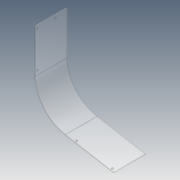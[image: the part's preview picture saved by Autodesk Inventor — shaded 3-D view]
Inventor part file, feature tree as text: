
AUTODESK INVENTOR PART (.ipt)
format: ipt  version: 2012 (Build 160160000, 160)  size: 96,256 bytes
history: native  units: in
note: dims shown in document units (in); Inventor stores cm internally (conversion verified against a paired STEP export)
features: pattern_linear x3, hole x2, extrude x1, sketch x1, reference x1
ambient origin geometry x8: Origin, YZ Plane, XZ Plane, XY Plane, X Axis, Y Axis, Z Axis, Center Point
bodies: Solid1 (feature_tree)
feature tree (8):
  extrude  "Extrusion1"  Depth=0.5in
  hole  "Hole1"  [1 undecoded]
  pattern_linear  "Rectangular Pattern1"  Count1=2 Spacing1=2.6875in
  pattern_linear  "Rectangular Pattern2"  Spacing1=0.5in  [1 undecoded]
  hole  "Hole2"  [1 undecoded]
  pattern_linear  "Rectangular Pattern4"  [2 undecoded]
  sketch  "Sketch1"  dims[d0=4.625in d1=0.0in d2=0.5in d3=0.3125in d4=0.265in d5=0.75in d6=0.375in d7=0.25in d8=0.5635in d9=1.0in d10=0.8108in d11=0.7874in d13=5.25in d14=0.7874in d16=2.6875in d17=0.5in d18=0.3125in d19=0.265in d20=0.75in d21=0.375in d22=0.25in d23=0.5635in d24=1.0in d25=0.8108in d29=0.7874in d31=5.25in]
  reference  "Reference1"
note: 5 required parameter values undecoded (feature->parameter linkage not recoverable at this tier; creation-order binding heuristic only, values carry confidence <= 0.55)
